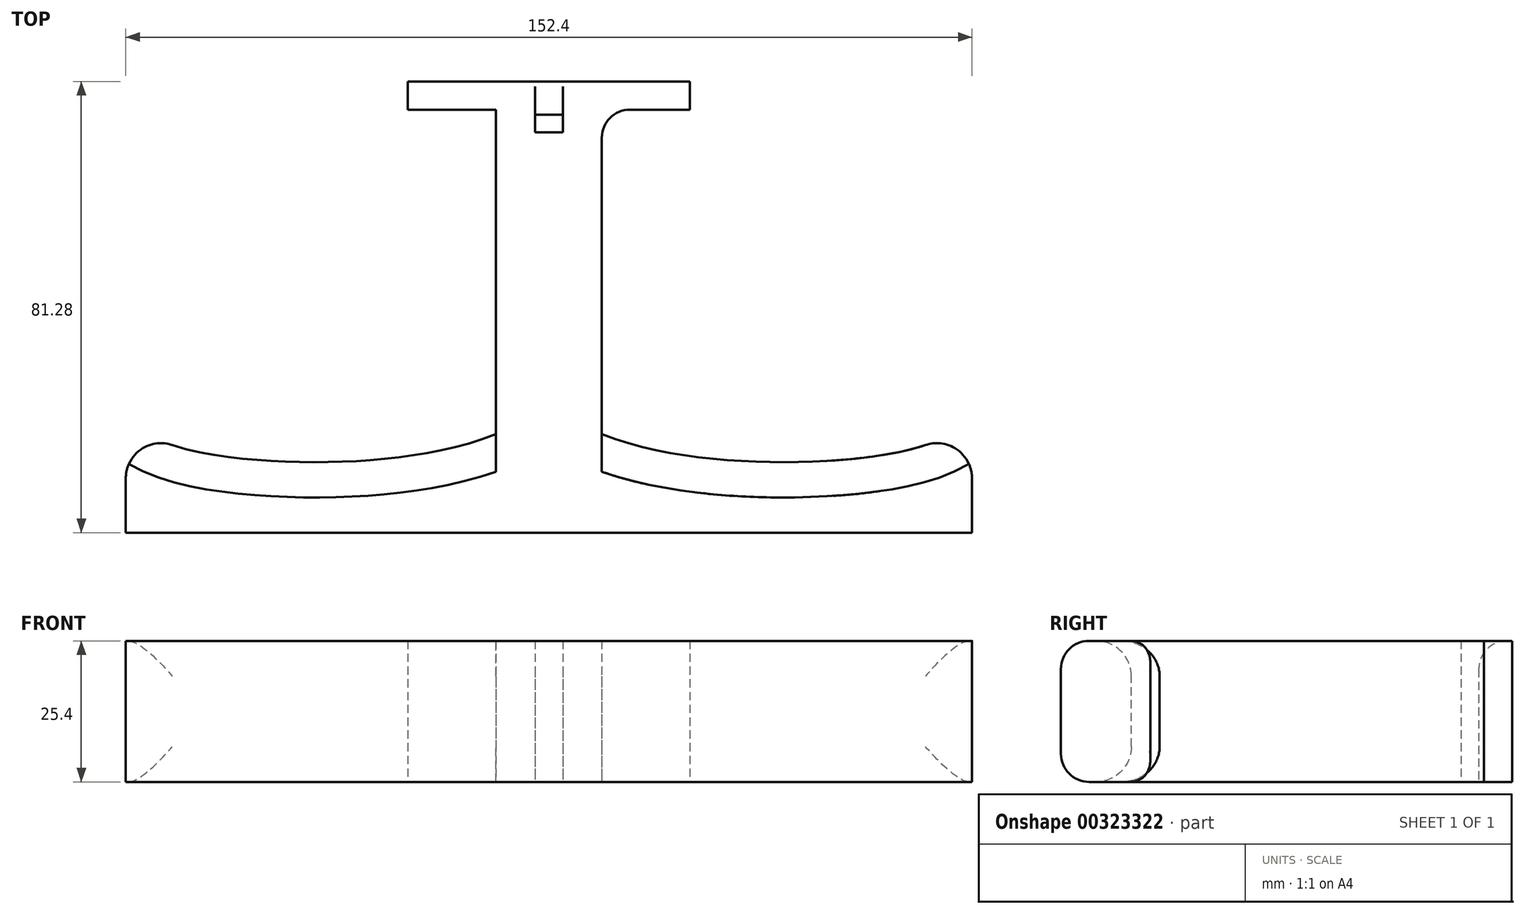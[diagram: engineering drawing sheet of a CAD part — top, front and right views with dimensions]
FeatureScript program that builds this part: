
annotation { "Feature Type Name" : "Feature", "Feature Type Description" : "" }
export const myFeature = defineFeature(function(context is Context, id is Id, definition is map)
    precondition{}
    {
        {
            var Q0;
            Q0=qCreatedBy(makeId("Top.planeOp"),FACE);
            var sketch = newSketch(context, id + "F0", { "sketchPlane" : qUnion([Q0])});
            skLineSegment(sketch, "E0", {"start": v(0, 0) * mm, "end": v(0, 76.2) * mm, "construction": true});
            skLineSegment(sketch, "E1", {"start": v(0, 0) * mm, "end": v(-76.2, 0) * mm});
            skLineSegment(sketch, "E2", {"start": v(-76.2, 0) * mm, "end": v(-76.2, 20.32) * mm});
            skLineSegment(sketch, "E3", {"start": v(0, 76.2) * mm, "end": v(-9.53, 76.2) * mm});
            skLineSegment(sketch, "E4", {"start": v(-9.53, 76.2) * mm, "end": v(-9.52, 17.78) * mm});
            skFitSpline(sketch, "E5", {"points": [v(-76.2, 20.32) * mm, v(-66.49, 15.36) * mm, v(-9.52, 17.78) * mm], "startDerivative": vector(17.64, -11.43) * mm, "endDerivative": vector(68.2, 28.52) * mm});
            skLineSegment(sketch, "E6.MirrorCS", {"start": v(0, 0) * mm, "end": v(76.2, 0) * mm});
            skLineSegment(sketch, "E7.MirrorCS", {"start": v(76.2, 0) * mm, "end": v(76.2, 20.32) * mm});
            skLineSegment(sketch, "E8.MirrorCS", {"start": v(0, 76.2) * mm, "end": v(9.53, 76.2) * mm});
            skLineSegment(sketch, "E9.MirrorCS", {"start": v(9.53, 76.2) * mm, "end": v(9.52, 17.78) * mm});
            skFitSpline(sketch, "E10.MirrorCS", {"points": [v(76.2, 20.32) * mm, v(66.49, 15.36) * mm, v(9.52, 17.78) * mm], "startDerivative": vector(-17.64, -11.43) * mm, "endDerivative": vector(-68.2, 28.52) * mm});
            skSolve(sketch);
        }
        {
            var Q0;
            Q0 = qSketchRegion(id + "F0", true);
            extrude(context, id + "F1", {"entities" : qUnion([Q0]), "depth" : 25.4 * mm});
        }
        {
            var Q0;
            Q0=makeQuery(id+"F1.opExtrude","CAP_EDGE",EDGE,{"disambiguationData":[OSD([sQuery(id+"F0.wireOp",EDGE,"E5")])],"isStart":false});
            var Q1;
            Q1=makeQuery(id+"F1.opExtrude","CAP_EDGE",EDGE,{"disambiguationData":[OSD([sQuery(id+"F0.wireOp",EDGE,"E5")])],"isStart":true});
            var Q2;
            Q2=makeQuery(id+"F1.opExtrude","CAP_EDGE",EDGE,{"disambiguationData":[OSD([sQuery(id+"F0.wireOp",EDGE,"E10.MirrorCS")])],"isStart":true});
            var Q3;
            Q3=makeQuery(id+"F1.opExtrude","CAP_EDGE",EDGE,{"disambiguationData":[OSD([sQuery(id+"F0.wireOp",EDGE,"E10.MirrorCS")])],"isStart":false});
            var Q4;
            Q4=makeQuery(id+"F1.opExtrude","SWEPT_EDGE",EDGE,{"disambiguationData":[OSD([sQuery(id+"F0.wireOp",EDGE,"E7.MirrorCS"),sQuery(id+"F0.wireOp",EDGE,"E10.MirrorCS")])]});
            var Q5;
            Q5=makeQuery(id+"F1.opExtrude","SWEPT_EDGE",EDGE,{"disambiguationData":[OSD([sQuery(id+"F0.wireOp",EDGE,"E2"),sQuery(id+"F0.wireOp",EDGE,"E5")])]});
            fillet(context, id + "F2", {"entities" : qUnion([Q0, Q1, Q2, Q3, Q4, Q5]), "radius" : 6.35 * mm, "tangentPropagation" : true, "allowEdgeOverflow" : false});
        }
        {
            var Q0;
            Q0=makeQuery(id+"F1.opExtrude","SWEPT_FACE",FACE,{"disambiguationData":[OSD([sQuery(id+"F0.wireOp",EDGE,"E3"),sQuery(id+"F0.wireOp",EDGE,"E8.MirrorCS")])]});
            var sketch = newSketch(context, id + "F3", { "sketchPlane" : qUnion([Q0])});
            skLineSegment(sketch, "E11", {"start": v(0, 25.4) * mm, "end": v(0, 0) * mm, "construction": true});
            skLineSegment(sketch, "E12", {"start": v(0, 25.4) * mm, "end": v(-25.4, 25.4) * mm});
            skLineSegment(sketch, "E13", {"start": v(-25.4, 25.4) * mm, "end": v(-25.4, 0) * mm});
            skLineSegment(sketch, "E14", {"start": v(-25.4, 0) * mm, "end": v(0, 0) * mm});
            skLineSegment(sketch, "E15.MirrorCS", {"start": v(0, 25.4) * mm, "end": v(25.4, 25.4) * mm});
            skLineSegment(sketch, "E16.MirrorCS", {"start": v(25.4, 25.4) * mm, "end": v(25.4, 0) * mm});
            skLineSegment(sketch, "E17.MirrorCS", {"start": v(25.4, 0) * mm, "end": v(0, 0) * mm});
            skSolve(sketch);
        }
        {
            var Q0;
            Q0 = qSketchRegion(id + "F3", true);
            extrude(context, id + "F4", {"entities" : qUnion([Q0]), "operationType" : NewBodyOperationType.ADD, "depth" : 5.08 * mm});
        }
        {
            var Q0;
            Q0=makeQuery(id+"F4.boolean.opBoolean","MERGE",FACE,{"derivedFrom":[makeQuery(id+"F1.opExtrude","CAP_FACE",FACE,{"disambiguationData":[OSD([sQuery(id+"F0.wireOp",EDGE,"E1"),sQuery(id+"F0.wireOp",EDGE,"E2"),sQuery(id+"F0.wireOp",EDGE,"E3"),sQuery(id+"F0.wireOp",EDGE,"E4"),sQuery(id+"F0.wireOp",EDGE,"E5"),sQuery(id+"F0.wireOp",EDGE,"E6.MirrorCS"),sQuery(id+"F0.wireOp",EDGE,"E7.MirrorCS"),sQuery(id+"F0.wireOp",EDGE,"E8.MirrorCS"),sQuery(id+"F0.wireOp",EDGE,"E9.MirrorCS"),sQuery(id+"F0.wireOp",EDGE,"E10.MirrorCS")])],"isStart":true}),makeQuery(id+"F4.opExtrude","SWEPT_FACE",FACE,{"disambiguationData":[OSD([sQuery(id+"F3.wireOp",EDGE,"E14"),sQuery(id+"F3.wireOp",EDGE,"E17.MirrorCS")])]})]});
            var sketch = newSketch(context, id + "F5", { "sketchPlane" : qUnion([Q0])});
            skPoint(sketch, "E18.centerSnap0", {"position": v(0, -81.28) * mm});
            skLineSegment(sketch, "E19", {"start": v(0, -81.28) * mm, "end": v(0, -60.8) * mm, "construction": true});
            skLineSegment(sketch, "E20", {"start": v(0, -75.25) * mm, "end": v(-2.5, -75.25) * mm});
            skLineSegment(sketch, "E21", {"start": v(-2.5, -75.25) * mm, "end": v(-2.5, -72.07) * mm});
            skLineSegment(sketch, "E22", {"start": v(-2.5, -72.07) * mm, "end": v(0, -72.07) * mm});
            skPoint(sketch, "E22.endSnap0", {"position": v(0, -71.04) * mm});
            skLineSegment(sketch, "E23.MirrorCS", {"start": v(0, -75.25) * mm, "end": v(2.5, -75.25) * mm});
            skLineSegment(sketch, "E24.MirrorCS", {"start": v(2.5, -75.25) * mm, "end": v(2.5, -72.07) * mm});
            skLineSegment(sketch, "E25.MirrorCS", {"start": v(2.5, -72.07) * mm, "end": v(0, -72.07) * mm});
            skSolve(sketch);
        }
        {
            var Q0;
            Q0 = qSketchRegion(id + "F5", true);
            extrude(context, id + "F6", {"entities" : qUnion([Q0]), "operationType" : NewBodyOperationType.REMOVE, "endBound" : BoundingType.THROUGH_ALL, "oppositeDirection" : true, "depth" : 25.4 * mm});
        }
        {
            var Q0;
            Q0=makeQuery(id+"F1.opExtrude","SWEPT_EDGE",EDGE,{"disambiguationData":[OSD([sQuery(id+"F0.wireOp",EDGE,"E8.MirrorCS"),sQuery(id+"F0.wireOp",EDGE,"E9.MirrorCS")])]});
            var Q1;
            Q1=makeQuery(id+"F1.opExtrude","SWEPT_EDGE",EDGE,{"disambiguationData":[OSD([sQuery(id+"F0.wireOp",EDGE,"E3"),sQuery(id+"F0.wireOp",EDGE,"E4")])]});
            var Q2;
            Q2=makeQuery(id+"F1.opExtrude","CAP_EDGE",EDGE,{"disambiguationData":[OSD([sQuery(id+"F0.wireOp",EDGE,"E1"),sQuery(id+"F0.wireOp",EDGE,"E6.MirrorCS")])],"isStart":true});
            var Q3;
            Q3=makeQuery(id+"F1.opExtrude","CAP_EDGE",EDGE,{"disambiguationData":[OSD([sQuery(id+"F0.wireOp",EDGE,"E1"),sQuery(id+"F0.wireOp",EDGE,"E6.MirrorCS")])],"isStart":false});
            var Q4;
            Q4=makeQuery(id+"F6.boolean.opBoolean","COPY",EDGE,{"derivedFrom":makeQuery(id+"F6.opExtrude","CAP_EDGE",EDGE,{"disambiguationData":[OSD([sQuery(id+"F5.wireOp",EDGE,"E20"),sQuery(id+"F5.wireOp",EDGE,"E23.MirrorCS")])],"isStart":true})});
            var Q5;
            Q5=makeQuery(id+"F6.boolean.opBoolean","INTERSECT",EDGE,{"derivedFrom":[makeQuery(id+"F4.boolean.opBoolean","MERGE",FACE,{"derivedFrom":[makeQuery(id+"F1.opExtrude","CAP_FACE",FACE,{"disambiguationData":[OSD([sQuery(id+"F0.wireOp",EDGE,"E1"),sQuery(id+"F0.wireOp",EDGE,"E2"),sQuery(id+"F0.wireOp",EDGE,"E3"),sQuery(id+"F0.wireOp",EDGE,"E4"),sQuery(id+"F0.wireOp",EDGE,"E5"),sQuery(id+"F0.wireOp",EDGE,"E6.MirrorCS"),sQuery(id+"F0.wireOp",EDGE,"E7.MirrorCS"),sQuery(id+"F0.wireOp",EDGE,"E8.MirrorCS"),sQuery(id+"F0.wireOp",EDGE,"E9.MirrorCS"),sQuery(id+"F0.wireOp",EDGE,"E10.MirrorCS")])],"isStart":false}),makeQuery(id+"F4.opExtrude","SWEPT_FACE",FACE,{"disambiguationData":[OSD([sQuery(id+"F3.wireOp",EDGE,"E12"),sQuery(id+"F3.wireOp",EDGE,"E15.MirrorCS")])]})]}),makeQuery(id+"F6.opExtrude","SWEPT_FACE",FACE,{"disambiguationData":[OSD([sQuery(id+"F5.wireOp",EDGE,"E20"),sQuery(id+"F5.wireOp",EDGE,"E23.MirrorCS")])]})]});
            fillet(context, id + "F7", {"entities" : qUnion([Q0, Q1, Q2, Q3, Q4, Q5]), "radius" : 5.08 * mm, "tangentPropagation" : true, "allowEdgeOverflow" : false});
        }
    });
